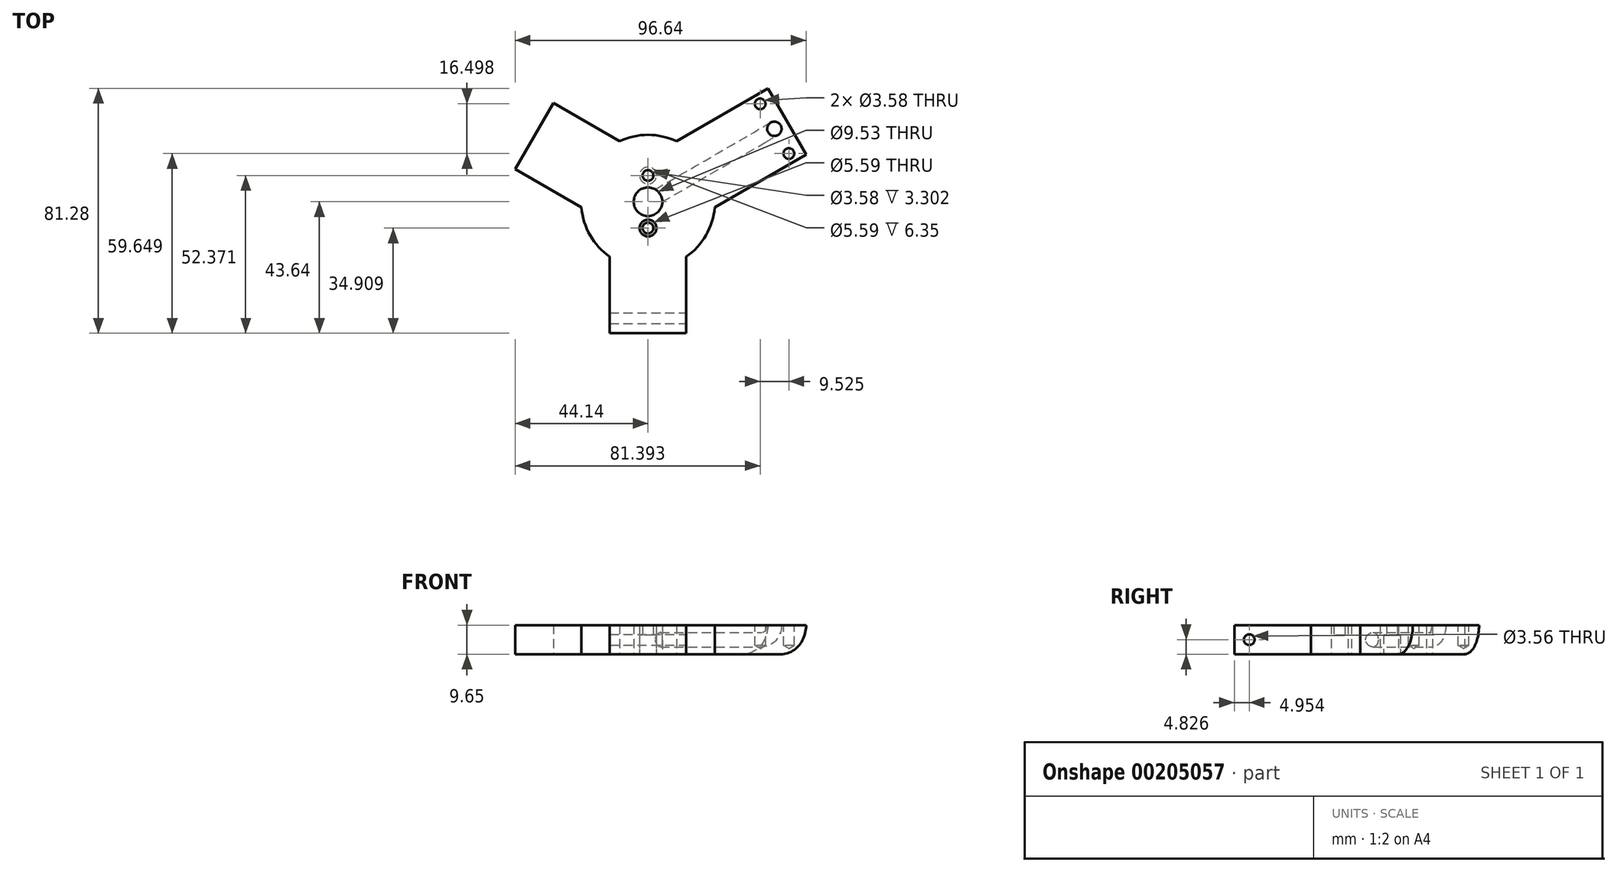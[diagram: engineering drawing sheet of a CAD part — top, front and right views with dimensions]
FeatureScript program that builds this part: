
annotation { "Feature Type Name" : "Feature", "Feature Type Description" : "" }
export const myFeature = defineFeature(function(context is Context, id is Id, definition is map)
    precondition{}
    {
        {
            var Q0;
            Q0=qCreatedBy(makeId("Top.planeOp"),FACE);
            var sketch = newSketch(context, id + "F0", { "sketchPlane" : qUnion([Q0])});
            skCircle(sketch, "E0", {"center": v(0, 0) * mm, "radius": 22.22 * mm});
            skLineSegment(sketch, "E1.top", {"start": v(12.7, -43.64) * mm, "end": v(-12.7, -43.64) * mm});
            skLineSegment(sketch, "E1.left", {"start": v(12.7, -18.24) * mm, "end": v(12.7, -43.64) * mm});
            skLineSegment(sketch, "E1.right", {"start": v(-12.7, -18.24) * mm, "end": v(-12.7, -43.64) * mm});
            skPoint(sketch, "E1.middle", {"position": v(0, -22.22) * mm});
            skPoint(sketch, "E2.orphan", {"position": v(-12.7, -0.81) * mm});
            skPoint(sketch, "E3.orphan", {"position": v(12.7, -0.81) * mm});
            skCircle(sketch, "E4", {"center": v(0, 0) * mm, "radius": 12.7 * mm});
            skLineSegment(sketch, "E5.1.0", {"start": v(22.15, -1.88) * mm, "end": v(44.14, 10.82) * mm});
            skLineSegment(sketch, "E5.1.1", {"start": v(31.44, 32.82) * mm, "end": v(44.14, 10.82) * mm});
            skLineSegment(sketch, "E5.1.2", {"start": v(9.45, 20.12) * mm, "end": v(31.44, 32.82) * mm});
            skLineSegment(sketch, "E5.2.0", {"start": v(-9.45, 20.12) * mm, "end": v(-31.44, 32.82) * mm});
            skLineSegment(sketch, "E5.2.1", {"start": v(-44.14, 10.82) * mm, "end": v(-31.44, 32.82) * mm});
            skLineSegment(sketch, "E5.2.2", {"start": v(-22.15, -1.88) * mm, "end": v(-44.14, 10.82) * mm});
            skCircle(sketch, "E6", {"center": v(0, 0) * mm, "radius": 4.76 * mm});
            skLineSegment(sketch, "E7", {"start": v(0, 12.7) * mm, "end": v(0, 4.76) * mm, "construction": true});
            skLineSegment(sketch, "E8", {"start": v(-4.76, 0) * mm, "end": v(4.76, 0) * mm, "construction": true});
            skCircle(sketch, "E9", {"center": v(0, 8.73) * mm, "radius": 1.8 * mm});
            skCircle(sketch, "E10", {"center": v(0, 8.73) * mm, "radius": 2.8 * mm});
            skCircle(sketch, "E11.MirrorC", {"center": v(0, -8.73) * mm, "radius": 1.8 * mm});
            skCircle(sketch, "E12.MirrorC", {"center": v(0, -8.73) * mm, "radius": 2.8 * mm});
            skSolve(sketch);
        }
        {
            var Q0;
            {var subQ0=sQuery(id+"F0.wireOp",EDGE,"E5.2.0");Q0=makeQuery(id+"F0.imprint","IMPRINT",FACE,{"disambiguationData":[TD([[makeQuery(id+"F0.imprint","IMPRINT",EDGE,{"derivedFrom":subQ0}),1.0]])]});}
            var Q1;
            Q1=makeQuery(id+"F0.imprint","IMPRINT",FACE,{"disambiguationData":[TD([[makeQuery(id+"F0.imprint","IMPRINT",EDGE,{"derivedFrom":sQuery(id+"F0.wireOp",EDGE,"E4")}),-1.0]])]});
            var Q2;
            Q2=makeQuery(id+"F0.imprint","IMPRINT",FACE,{"disambiguationData":[TD([[makeQuery(id+"F0.imprint","IMPRINT",EDGE,{"derivedFrom":sQuery(id+"F0.wireOp",EDGE,"E1.top")}),-1.0]])]});
            var Q3;
            {var subQ0=sQuery(id+"F0.wireOp",EDGE,"E5.1.0");Q3=makeQuery(id+"F0.imprint","IMPRINT",FACE,{"disambiguationData":[TD([[makeQuery(id+"F0.imprint","IMPRINT",EDGE,{"derivedFrom":subQ0}),1.0]])]});}
            var Q4;
            {var subQ0=sQuery(id+"F0.wireOp",EDGE,"mpykQxPc-7yeO-fXCO-FtW2-F6NX8IxqQ4yY");Q4=makeQuery(id+"F0.imprint","IMPRINT",FACE,{"disambiguationData":[TD([[makeQuery(id+"F0.imprint","IMPRINT",EDGE,{"derivedFrom":subQ0}),1.0]])]});}
            var Q5;
            Q5=makeQuery(id+"F0.imprint","IMPRINT",FACE,{"disambiguationData":[TD([[makeQuery(id+"F0.imprint","IMPRINT",EDGE,{"derivedFrom":sQuery(id+"F0.wireOp",EDGE,"E4")}),1.0]])]});
            var Q6;
            Q6=makeQuery(id+"F0.imprint","IMPRINT",FACE,{"disambiguationData":[TD([[makeQuery(id+"F0.imprint","IMPRINT",EDGE,{"derivedFrom":sQuery(id+"F0.wireOp",EDGE,"E9")}),-1.0]])]});
            var Q7;
            Q7=makeQuery(id+"F0.imprint","IMPRINT",FACE,{"disambiguationData":[TD([[makeQuery(id+"F0.imprint","IMPRINT",EDGE,{"derivedFrom":sQuery(id+"F0.wireOp",EDGE,"E11.MirrorC")}),1.0]])]});
            extrude(context, id + "F1", {"entities" : qUnion([Q0, Q1, Q2, Q3, Q4, Q5, Q6, Q7]), "depth" : 9.65 * mm});
        }
        {
            var Q0;
            Q0=makeQuery(id+"F0.imprint","IMPRINT",FACE,{"disambiguationData":[TD([[makeQuery(id+"F0.imprint","IMPRINT",EDGE,{"derivedFrom":sQuery(id+"F0.wireOp",EDGE,"E9")}),-1.0]])]});
            var Q1;
            Q1=makeQuery(id+"F0.imprint","IMPRINT",FACE,{"disambiguationData":[TD([[makeQuery(id+"F0.imprint","IMPRINT",EDGE,{"derivedFrom":sQuery(id+"F0.wireOp",EDGE,"E11.MirrorC")}),1.0]])]});
            extrude(context, id + "F2", {"entities" : qUnion([Q0, Q1]), "operationType" : NewBodyOperationType.REMOVE, "depth" : 6.35 * mm});
        }
        {
            var Q0;
            Q0=makeQuery(id+"F1.opExtrude","SWEPT_FACE",FACE,{"disambiguationData":[OSD([sQuery(id+"F0.wireOp",EDGE,"E5.1.1")])]});
            var sketch = newSketch(context, id + "F3", { "sketchPlane" : qUnion([Q0])});
            skCircle(sketch, "E13", {"center": v(0, 4.83) * mm, "radius": 2.39 * mm});
            skPoint(sketch, "E13.centerSnap0", {"position": v(12.7, 4.83) * mm});
            skLineSegment(sketch, "E14.bottom", {"start": v(12.7, 0) * mm, "end": v(-12.7, 0) * mm});
            skLineSegment(sketch, "E14.top", {"start": v(12.7, 9.65) * mm, "end": v(-12.7, 9.65) * mm});
            skLineSegment(sketch, "E14.left", {"start": v(12.7, 0) * mm, "end": v(12.7, 9.65) * mm});
            skLineSegment(sketch, "E14.right", {"start": v(-12.7, 0) * mm, "end": v(-12.7, 9.65) * mm});
            skSolve(sketch);
        }
        {
            var Q0;
            Q0=makeQuery(id+"F3.imprint","IMPRINT",FACE,{"disambiguationData":[TD([[makeQuery(id+"F3.imprint","IMPRINT",EDGE,{"derivedFrom":sQuery(id+"F3.wireOp",EDGE,"E13")}),1.0]])]});
            extrude(context, id + "F4", {"entities" : qUnion([Q0]), "operationType" : NewBodyOperationType.REMOVE, "oppositeDirection" : true, "depth" : 41.17 * mm});
        }
        {
            var Q0;
            Q0=makeQuery(id+"F1.opExtrude","SWEPT_FACE",FACE,{"disambiguationData":[OSD([sQuery(id+"F0.wireOp",EDGE,"E5.1.1")])]});
            var Q1;
            Q1=makeQuery(id+"F1.opExtrude","CAP_EDGE",EDGE,{"disambiguationData":[OSD([sQuery(id+"F0.wireOp",EDGE,"E5.1.1")])],"isStart":false});
            revolve(context, id + "F5", {"operationType" : NewBodyOperationType.ADD, "entities" : qUnion([Q0]), "axis" : qUnion([Q1]), "revolveType" : RevolveType.ONE_DIRECTION, "angle" : 90 * degree});
        }
        {
            var Q0;
            Q0=makeQuery(id+"F3.imprint","IMPRINT",FACE,{"disambiguationData":[TD([[makeQuery(id+"F3.imprint","IMPRINT",EDGE,{"derivedFrom":sQuery(id+"F3.wireOp",EDGE,"E13")}),1.0]])]});
            extrude(context, id + "F6", {"entities" : qUnion([Q0]), "operationType" : NewBodyOperationType.REMOVE, "oppositeDirection" : true, "depth" : 41.43 * mm});
        }
        {
            var Q0;
            Q0=makeQuery(id+"F1.opExtrude","SWEPT_FACE",FACE,{"disambiguationData":[OSD([sQuery(id+"F0.wireOp",EDGE,"E1.left")])]});
            var sketch = newSketch(context, id + "F7", { "sketchPlane" : qUnion([Q0])});
            skCircle(sketch, "E15", {"center": v(-38.69, 4.83) * mm, "radius": 1.78 * mm});
            skPoint(sketch, "E15.centerSnap0", {"position": v(-43.64, 4.83) * mm});
            skSolve(sketch);
        }
        {
            var Q0;
            Q0=makeQuery(id+"F7.imprint","IMPRINT",FACE,{"disambiguationData":[TD([[makeQuery(id+"F7.imprint","IMPRINT",EDGE,{"derivedFrom":sQuery(id+"F7.wireOp",EDGE,"E15")}),1.0]])]});
            extrude(context, id + "F8", {"entities" : qUnion([Q0]), "operationType" : NewBodyOperationType.REMOVE, "oppositeDirection" : true, "depth" : 25.4 * mm});
        }
        {
            var Q0;
            {var subQ0=sQuery(id+"F0.wireOp",EDGE,"E5.1.1");Q0=makeQuery(id+"FtxmlhN4hyiTaTl_1.boolean.opBoolean","MERGE",FACE,{"derivedFrom":[makeQuery(id+"F1.opExtrude","CAP_FACE",FACE,{"disambiguationData":[OSD([sQuery(id+"F0.wireOp",EDGE,"E0"),sQuery(id+"F0.wireOp",EDGE,"E1.top"),sQuery(id+"F0.wireOp",EDGE,"E1.left"),sQuery(id+"F0.wireOp",EDGE,"E1.right"),sQuery(id+"F0.wireOp",EDGE,"E5.1.0"),subQ0,sQuery(id+"F0.wireOp",EDGE,"E5.1.2"),sQuery(id+"F0.wireOp",EDGE,"E5.2.0"),sQuery(id+"F0.wireOp",EDGE,"E5.2.1"),sQuery(id+"F0.wireOp",EDGE,"E5.2.2"),sQuery(id+"F0.wireOp",EDGE,"E6"),sQuery(id+"F0.wireOp",EDGE,"E9"),sQuery(id+"F0.wireOp",EDGE,"E11.MirrorC")])],"isStart":false}),makeQuery(id+"FtxmlhN4hyiTaTl_1.opRevolve","CAP_FACE",FACE,{"disambiguationData":[OSD([subQ0])],"isStart":false})]});}
            var sketch = newSketch(context, id + "F9", { "sketchPlane" : qUnion([Q0])});
            skPoint(sketch, "E16", {"position": v(46.78, 16) * mm});
            skPoint(sketch, "E17", {"position": v(37.25, 32.5) * mm});
            skLineSegment(sketch, "E18", {"start": v(31.44, 32.82) * mm, "end": v(44.14, 10.82) * mm});
            skSolve(sketch);
        }
        {
            var Q0;
            Q0=sQuery(id+"F9.wireOp",VERTEX,"E17");
            var Q1;
            Q1=sQuery(id+"F9.wireOp",VERTEX,"E16");
            var Q2;
            Q2=makeQuery(id+"F1.opExtrude","SWEPT_BODY",BODY,{"disambiguationData":[OSD([sQuery(id+"F0.wireOp",EDGE,"E0"),sQuery(id+"F0.wireOp",EDGE,"E1.top"),sQuery(id+"F0.wireOp",EDGE,"E1.left"),sQuery(id+"F0.wireOp",EDGE,"E1.right"),sQuery(id+"F0.wireOp",EDGE,"E5.1.0"),sQuery(id+"F0.wireOp",EDGE,"E5.1.1"),sQuery(id+"F0.wireOp",EDGE,"E5.1.2"),sQuery(id+"F0.wireOp",EDGE,"E5.2.0"),sQuery(id+"F0.wireOp",EDGE,"E5.2.1"),sQuery(id+"F0.wireOp",EDGE,"E5.2.2"),sQuery(id+"F0.wireOp",EDGE,"E6"),sQuery(id+"F0.wireOp",EDGE,"E9"),sQuery(id+"F0.wireOp",EDGE,"E11.MirrorC")])]});
            hole(context, id + "F10", {"style" : HoleStyle.SIMPLE, "endStyle" : HoleEndStyle.BLIND, "holeDiameter" : 3.58 * mm, "holeDepth" : 6.73 * mm, "locations" : qUnion([Q0, Q1]), "scope" : qUnion([Q2])});
        }
    });
